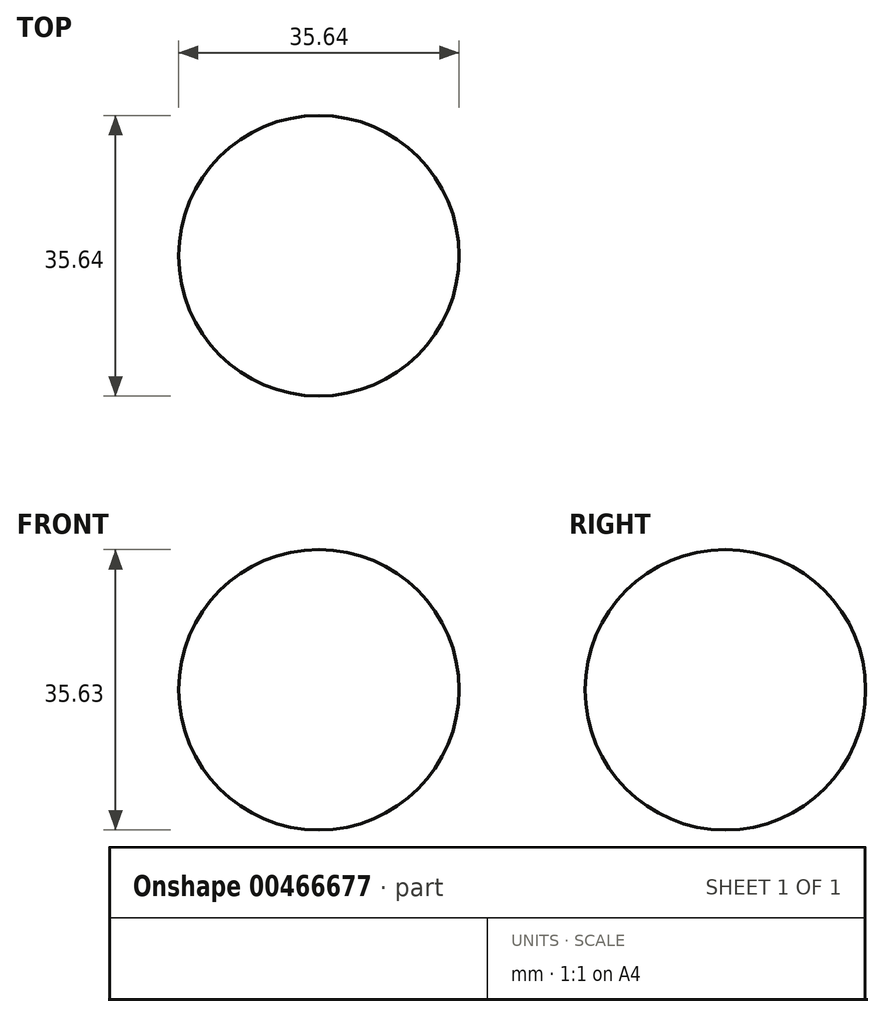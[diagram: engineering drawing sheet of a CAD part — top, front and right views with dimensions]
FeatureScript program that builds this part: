
annotation { "Feature Type Name" : "Feature", "Feature Type Description" : "" }
export const myFeature = defineFeature(function(context is Context, id is Id, definition is map)
    precondition{}
    {
        {
            var Q0;
            Q0=qCreatedBy(makeId("Front.planeOp"),FACE);
            var sketch = newSketch(context, id + "F0", { "sketchPlane" : qUnion([Q0])});
            skCircle(sketch, "E0", {"center": v(0, 27.8) * mm, "radius": 17.82 * mm});
            skCircle(sketch, "E1", {"center": v(38.88, 0) * mm, "radius": 12.37 * mm});
            skCircle(sketch, "E2", {"center": v(-32.42, -24.52) * mm, "radius": 17.08 * mm});
            skLineSegment(sketch, "E3", {"start": v(0, 52.57) * mm, "end": v(0, 0) * mm});
            skSolve(sketch);
        }
        {
            var Q0;
            {var subQ0=sQuery(id+"F0.wireOp",EDGE,"E3");var subQ1=sQuery(id+"F0.wireOp",EDGE,"E0");var subQ2=makeQuery(id+"F0.imprint","INTERSECT",VERTEX,{"disambiguationData":[OD(0.0)],"derivedFrom":[subQ1,subQ0]});Q0=makeQuery(id+"F0.imprint","IMPRINT",FACE,{"disambiguationData":[TD([[makeQuery(id+"F0.imprint","IMPRINT",EDGE,{"disambiguationData":[TD([[subQ2,-1.0]])],"derivedFrom":subQ1}),1.0]])]});}
            var Q1;
            Q1=sQuery(id+"F0.wireOp",EDGE,"E3");
            revolve(context, id + "F1", {"entities" : qUnion([Q0]), "axis" : qUnion([Q1]), "revolveType" : RevolveType.FULL});
        }
    });
